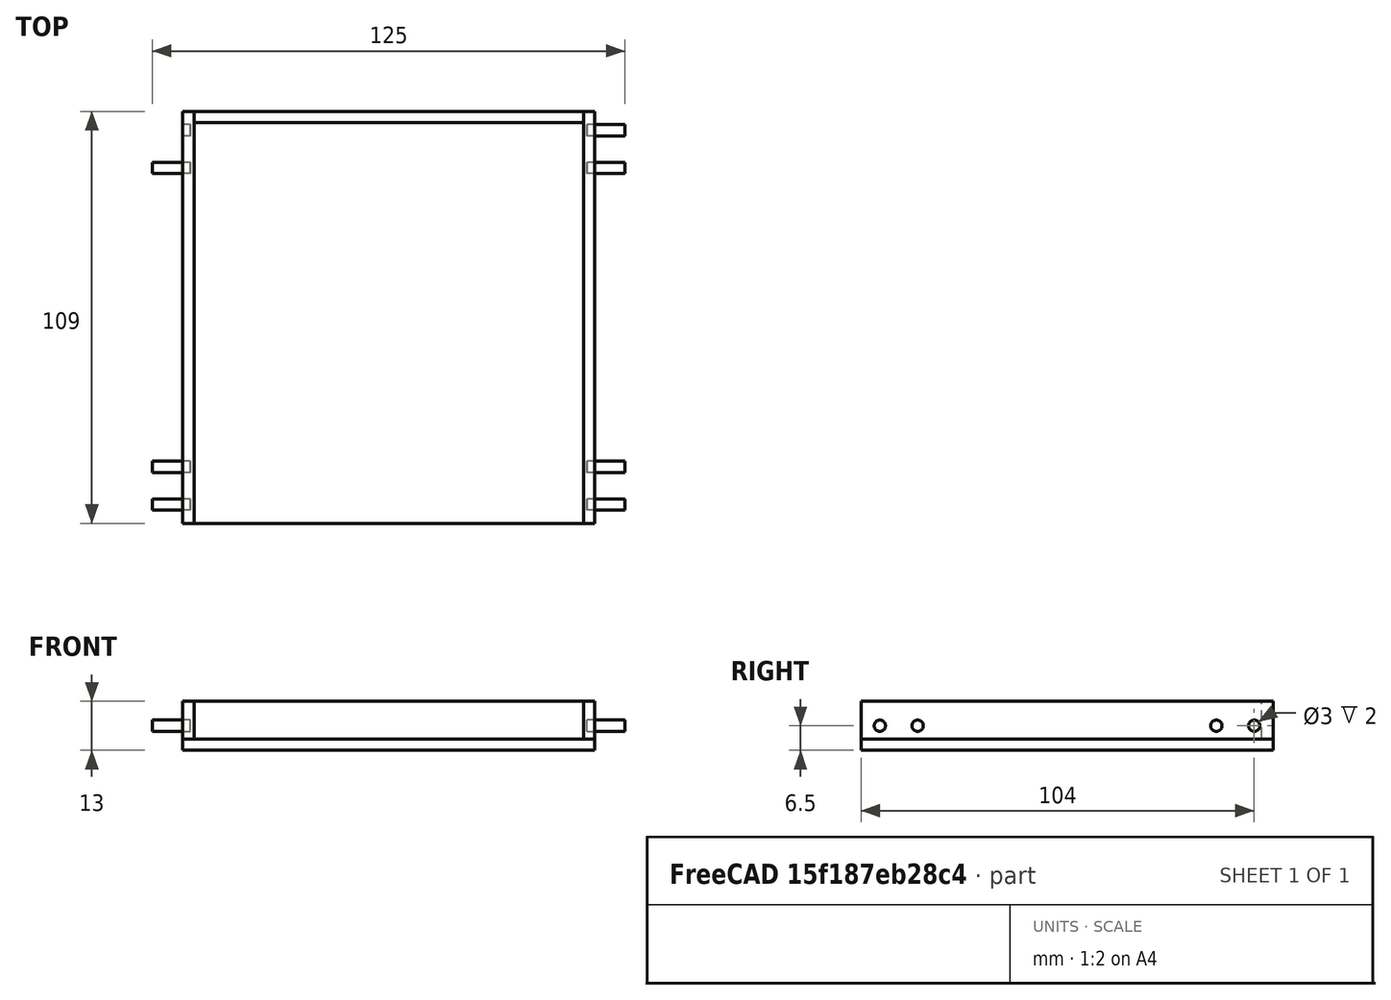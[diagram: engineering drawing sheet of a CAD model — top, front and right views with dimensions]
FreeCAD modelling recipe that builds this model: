
FCSTD DOCUMENT  (FreeCAD 0.20R29603 (Git))
Label: case_rev
License: All rights reserved
LicenseURL: http://en.wikipedia.org/wiki/All_rights_reserved
objects: Part::Cylinder×8, Part::Box×4, Part::Cut×1
note: 13 computed .brp shape members not serialized (recipe doc carries the construction recipe); baked Part::Feature solids carry a one-line shape summary decoded from their .brp

FEATURE [Part::Box] Box  label="Floor"
  AttacherType = Attacher::AttachEngine3D
  Height = 3
  Length = 109
  Width = 109
FEATURE [Part::Box] Box001  label="RWall"
  AttacherType = Attacher::AttachEngine3D
  Height = 10
  Length = 3
  Placement = pos=(0,0,3) rot=(0,0,1;0rad)
  Width = 109
FEATURE [Part::Box] Box002  label="LWall"
  AttacherType = Attacher::AttachEngine3D
  Height = 10
  Length = 3
  Placement = pos=(106,0,3) rot=(0,0,1;0rad)
  Width = 109
FEATURE [Part::Box] Box003  label="Back"
  AttacherType = Attacher::AttachEngine3D
  Height = 10
  Length = 103
  Placement = pos=(3,106,3) rot=(0,0,1;0rad)
  Width = 3
FEATURE [Part::Cylinder] Cylinder  label="Hole"
  Angle = 360
  AttacherType = Attacher::AttachEngine3D
  FirstAngle = 0
  Height = 10
  Placement = pos=(-8,5,6.5) rot=(0,1,0;1.5708rad)
  Radius = 1.5
  SecondAngle = 0
FEATURE [Part::Cylinder] Cylinder001  label="Hole001"
  Angle = 360
  AttacherType = Attacher::AttachEngine3D
  FirstAngle = 0
  Height = 10
  Placement = pos=(-8,104,6.5) rot=(0,1,0;1.5708rad)
  Radius = 1.5
  SecondAngle = 0
FEATURE [Part::Cylinder] Cylinder002  label="Hole002"
  Angle = 360
  AttacherType = Attacher::AttachEngine3D
  FirstAngle = 0
  Height = 10
  Placement = pos=(-8,15,6.5) rot=(0,1,0;1.5708rad)
  Radius = 1.5
  SecondAngle = 0
FEATURE [Part::Cylinder] Cylinder003  label="Hole003"
  Angle = 360
  AttacherType = Attacher::AttachEngine3D
  FirstAngle = 0
  Height = 10
  Placement = pos=(-8,94,6.5) rot=(0,1,0;1.5708rad)
  Radius = 1.5
  SecondAngle = 0
FEATURE [Part::Cylinder] Cylinder004  label="Hole004"
  Angle = 360
  AttacherType = Attacher::AttachEngine3D
  FirstAngle = 0
  Height = 10
  Placement = pos=(107,104,6.5) rot=(0,1,0;1.5708rad)
  Radius = 1.5
  SecondAngle = 0
FEATURE [Part::Cylinder] Cylinder005  label="Hole005"
  Angle = 360
  AttacherType = Attacher::AttachEngine3D
  FirstAngle = 0
  Height = 10
  Placement = pos=(107,94,6.5) rot=(0,1,0;1.5708rad)
  Radius = 1.5
  SecondAngle = 0
FEATURE [Part::Cylinder] Cylinder006  label="Hole006"
  Angle = 360
  AttacherType = Attacher::AttachEngine3D
  FirstAngle = 0
  Height = 10
  Placement = pos=(107,5,6.5) rot=(0,1,0;1.5708rad)
  Radius = 1.5
  SecondAngle = 0
FEATURE [Part::Cylinder] Cylinder007  label="Hole007"
  Angle = 360
  AttacherType = Attacher::AttachEngine3D
  FirstAngle = 0
  Height = 10
  Placement = pos=(107,15,6.5) rot=(0,1,0;1.5708rad)
  Radius = 1.5
  SecondAngle = 0
FEATURE [Part::Cut] Cut
  Base = -> Box001
  Tool = -> Cylinder001
